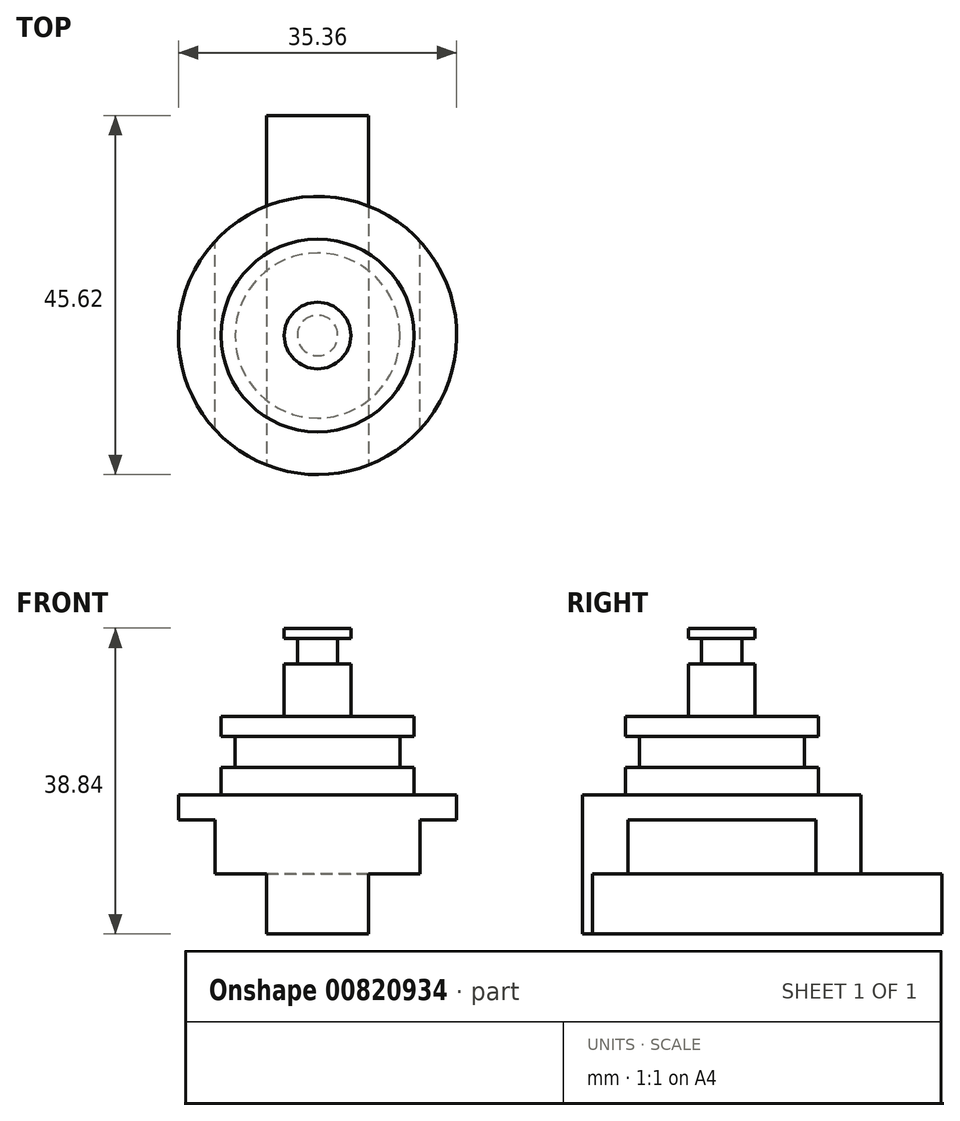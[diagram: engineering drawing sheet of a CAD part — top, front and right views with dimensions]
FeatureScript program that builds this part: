
annotation { "Feature Type Name" : "Feature", "Feature Type Description" : "" }
export const myFeature = defineFeature(function(context is Context, id is Id, definition is map)
    precondition{}
    {
        {
            var Q0;
            Q0=qCreatedBy(makeId("Front.planeOp"),FACE);
            var sketch = newSketch(context, id + "F0", { "sketchPlane" : qUnion([Q0])});
            skLineSegment(sketch, "E0", {"start": v(0, 0) * mm, "end": v(0, 21.2) * mm});
            skLineSegment(sketch, "E1", {"start": v(0, 0) * mm, "end": v(12.24, 0) * mm});
            skLineSegment(sketch, "E2", {"start": v(12.24, 0) * mm, "end": v(12.24, 3.54) * mm});
            skLineSegment(sketch, "E3", {"start": v(12.24, 3.54) * mm, "end": v(10.48, 3.54) * mm});
            skLineSegment(sketch, "E4", {"start": v(10.48, 3.54) * mm, "end": v(10.48, 7.48) * mm});
            skLineSegment(sketch, "E5", {"start": v(10.48, 7.48) * mm, "end": v(12.24, 7.48) * mm});
            skLineSegment(sketch, "E6", {"start": v(12.24, 7.48) * mm, "end": v(12.24, 10.02) * mm});
            skLineSegment(sketch, "E7", {"start": v(12.24, 10.02) * mm, "end": v(4.23, 10.02) * mm});
            skLineSegment(sketch, "E8", {"start": v(4.23, 10.02) * mm, "end": v(4.23, 16.65) * mm});
            skLineSegment(sketch, "E9", {"start": v(4.23, 16.65) * mm, "end": v(2.57, 16.65) * mm});
            skLineSegment(sketch, "E10", {"start": v(2.57, 16.65) * mm, "end": v(2.57, 19.93) * mm});
            skLineSegment(sketch, "E11", {"start": v(2.57, 19.93) * mm, "end": v(4.23, 19.93) * mm});
            skLineSegment(sketch, "E12", {"start": v(4.23, 19.93) * mm, "end": v(4.23, 21.2) * mm});
            skLineSegment(sketch, "E13", {"start": v(4.23, 21.2) * mm, "end": v(0, 21.2) * mm});
            skSolve(sketch);
        }
        {
            var Q0;
            Q0=makeQuery(id+"F0.imprint","IMPRINT",FACE,{"disambiguationData":[TD([[makeQuery(id+"F0.imprint","IMPRINT",EDGE,{"derivedFrom":sQuery(id+"F0.wireOp",EDGE,"E0")}),-1.0]])]});
            var Q1;
            Q1=sQuery(id+"F0.wireOp",EDGE,"E0");
            revolve(context, id + "F1", {"surfaceOperationType" : NewSurfaceOperationType.NEW, "entities" : qUnion([Q0]), "axis" : qUnion([Q1]), "revolveType" : RevolveType.FULL});
        }
        {
            var Q0;
            Q0=makeQuery(id+"F1.opRevolve","SWEPT_FACE",FACE,{"disambiguationData":[OSD([sQuery(id+"F0.wireOp",EDGE,"E1")])]});
            var sketch = newSketch(context, id + "F2", { "sketchPlane" : qUnion([Q0])});
            skCircle(sketch, "E14", {"center": v(0, 0) * mm, "radius": 17.68 * mm});
            skSolve(sketch);
        }
        {
            var Q0;
            Q0 = qSketchRegion(id + "F2", true);
            extrude(context, id + "F3", {"entities" : qUnion([Q0]), "operationType" : NewBodyOperationType.ADD, "depth" : 3.12 * mm, "offsetDistance" : 25.4 * mm});
        }
        {
            var Q0;
            Q0=makeQuery(id+"F3.opExtrude","CAP_FACE",FACE,{"disambiguationData":[OSD([sQuery(id+"F2.wireOp",EDGE,"E14")])],"isStart":false});
            var sketch = newSketch(context, id + "F4", { "sketchPlane" : qUnion([Q0])});
            skArc(sketch, "E15.0", {"start": v(-13.02, -11.96) * mm, "mid": v(0, -17.68) * mm, "end": v(13.02, -11.96) * mm});
            skLineSegment(sketch, "E16", {"start": v(-13.02, 11.96) * mm, "end": v(-13.02, -11.96) * mm});
            skLineSegment(sketch, "E17", {"start": v(13.02, 11.96) * mm, "end": v(13.02, -11.96) * mm});
            skLineSegment(sketch, "E18", {"start": v(0, 17.68) * mm, "end": v(0, -17.68) * mm, "construction": true});
            skArc(sketch, "E19.trimOffspring", {"start": v(13.02, 11.96) * mm, "mid": v(0, 17.68) * mm, "end": v(-13.02, 11.96) * mm});
            skSolve(sketch);
        }
        {
            var Q0;
            Q0 = qSketchRegion(id + "F4", true);
            extrude(context, id + "F5", {"entities" : qUnion([Q0]), "operationType" : NewBodyOperationType.ADD, "depth" : 6.9 * mm, "offsetDistance" : 25.4 * mm});
        }
        {
            var Q0;
            Q0=makeQuery(id+"F5.opExtrude","CAP_FACE",FACE,{"disambiguationData":[OSD([sQuery(id+"F4.wireOp",EDGE,"E15.0"),sQuery(id+"F4.wireOp",EDGE,"E16"),sQuery(id+"F4.wireOp",EDGE,"E17"),sQuery(id+"F4.wireOp",EDGE,"E19.trimOffspring")])],"isStart":false});
            var sketch = newSketch(context, id + "F6", { "sketchPlane" : qUnion([Q0])});
            skLineSegment(sketch, "E20.bottom", {"start": v(6.48, -27.94) * mm, "end": v(-6.48, -27.94) * mm});
            skLineSegment(sketch, "E20.left", {"start": v(6.48, -27.94) * mm, "end": v(6.48, 16.45) * mm});
            skLineSegment(sketch, "E20.right", {"start": v(-6.48, -27.94) * mm, "end": v(-6.48, 16.45) * mm});
            skPoint(sketch, "E20.middle", {"position": v(0, 0) * mm});
            skArc(sketch, "E21.0", {"start": v(6.48, 16.45) * mm, "mid": v(0, 17.68) * mm, "end": v(-6.48, 16.45) * mm});
            skLineSegment(sketch, "E22", {"start": v(0, -27.94) * mm, "end": v(0, 0) * mm, "construction": true});
            skSolve(sketch);
        }
        {
            var Q0;
            {var subQ0=sQuery(id+"F6.wireOp",EDGE,"E21.0");Q0=makeQuery(id+"F6.imprint","IMPRINT",FACE,{"disambiguationData":[TD([[makeQuery(id+"F6.imprint","IMPRINT",EDGE,{"derivedFrom":subQ0}),1.0]])]});}
            var Q1;
            {var subQ0=sQuery(id+"F6.wireOp",EDGE,"E20.bottom");Q1=makeQuery(id+"F6.imprint","IMPRINT",FACE,{"disambiguationData":[TD([[makeQuery(id+"F6.imprint","IMPRINT",EDGE,{"derivedFrom":subQ0}),-1.0]])]});}
            extrude(context, id + "F7", {"entities" : qUnion([Q0, Q1]), "operationType" : NewBodyOperationType.ADD, "depth" : 7.62 * mm, "offsetDistance" : 25.4 * mm});
        }
    });
